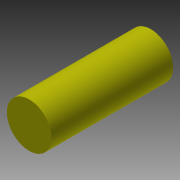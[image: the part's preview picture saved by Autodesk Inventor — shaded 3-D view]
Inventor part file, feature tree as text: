
AUTODESK INVENTOR PART (.ipt)
format: ipt  version: 2015 (Build 190159000, 159)  size: 80,896 bytes
history: native  units: mm
features: extrude x1, sketch x1
ambient origin geometry x8: Origin, YZ Plane, XZ Plane, XY Plane, X Axis, Y Axis, Z Axis, Center Point
bodies: Solid1 (feature_tree)
feature tree (2):
  extrude  "Extrusion1"  Depth=300.0mm TaperAngle=0.0deg
  sketch  "Sketch1"  dims[d0=110.0mm d1=300.0mm d2=0.0mm]
